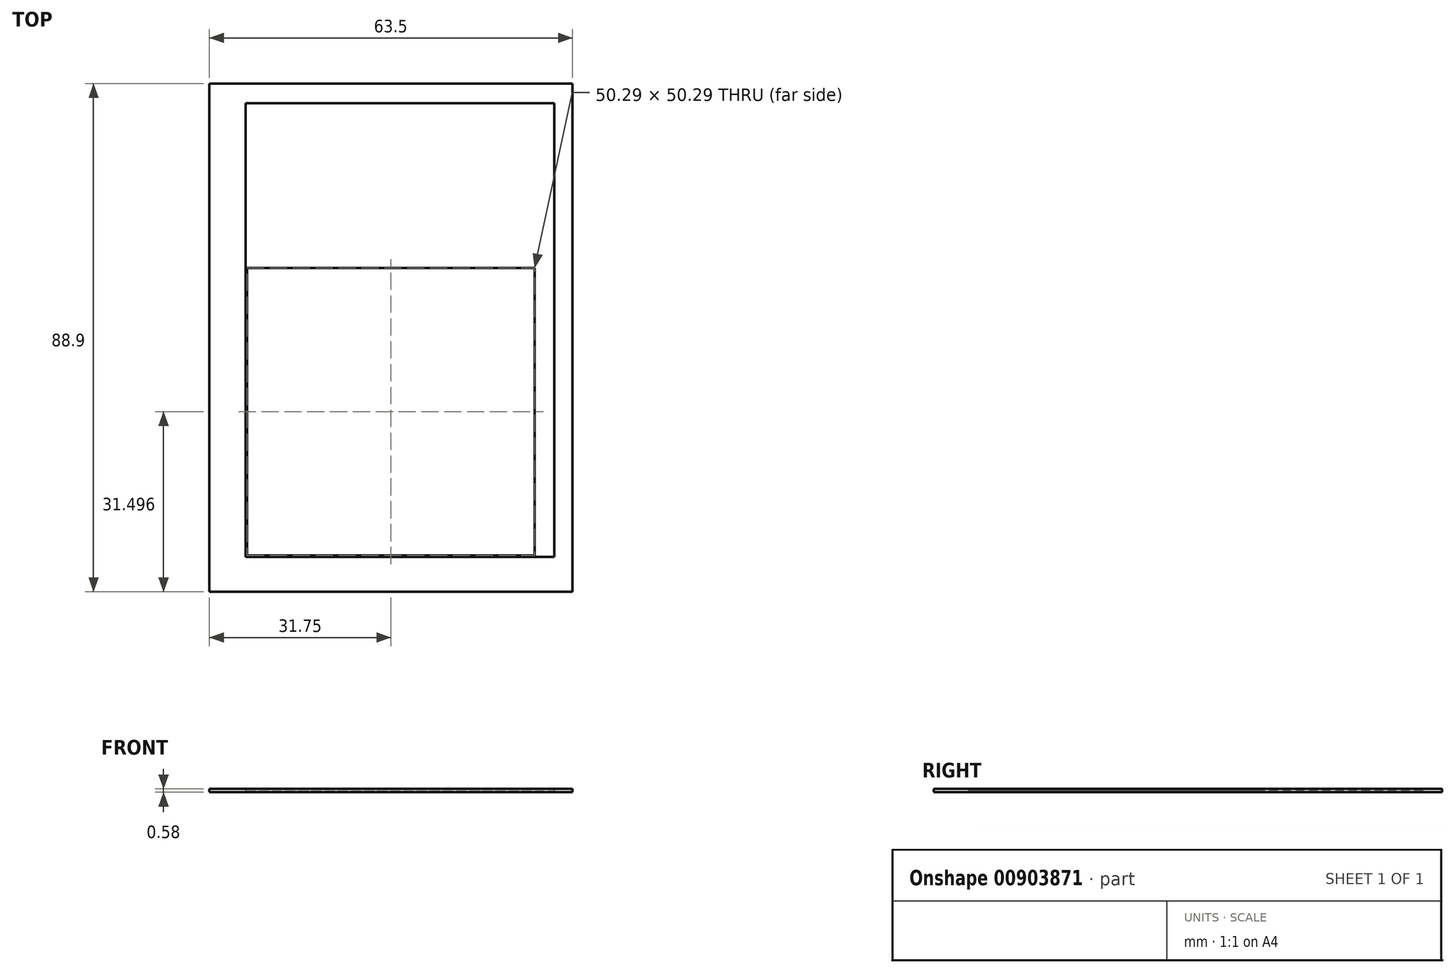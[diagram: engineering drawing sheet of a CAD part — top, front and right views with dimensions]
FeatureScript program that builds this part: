
annotation { "Feature Type Name" : "Feature", "Feature Type Description" : "" }
export const myFeature = defineFeature(function(context is Context, id is Id, definition is map)
    precondition{}
    {
        {
            var Q0;
            Q0=qCreatedBy(makeId("Top.planeOp"),FACE);
            var sketch = newSketch(context, id + "F0", { "sketchPlane" : qUnion([Q0])});
            skLineSegment(sketch, "E0.bottom", {"start": v(-25.15, 56.64) * mm, "end": v(25.15, 56.64) * mm});
            skLineSegment(sketch, "E0.top", {"start": v(-25.15, 6.35) * mm, "end": v(25.15, 6.35) * mm});
            skLineSegment(sketch, "E0.left", {"start": v(-25.15, 56.64) * mm, "end": v(-25.15, 6.35) * mm});
            skLineSegment(sketch, "E0.right", {"start": v(25.15, 56.64) * mm, "end": v(25.15, 6.35) * mm});
            skLineSegment(sketch, "E1.bottom", {"start": v(-31.75, 88.9) * mm, "end": v(31.75, 88.9) * mm});
            skLineSegment(sketch, "E1.top", {"start": v(-31.75, 0) * mm, "end": v(31.75, 0) * mm});
            skLineSegment(sketch, "E1.left", {"start": v(-31.75, 88.9) * mm, "end": v(-31.75, 0) * mm});
            skLineSegment(sketch, "E1.right", {"start": v(31.75, 88.9) * mm, "end": v(31.75, 0) * mm});
            skPoint(sketch, "E2", {"position": v(0, 88.9) * mm});
            skPoint(sketch, "E3", {"position": v(0, 56.64) * mm});
            skSolve(sketch);
        }
        {
            var Q0;
            Q0 = qSketchRegion(id + "F0", true);
            extrude(context, id + "F1", {"entities" : qUnion([Q0]), "depth" : 0.2 * mm, "offsetDistance" : 25.4 * mm});
        }
        {
            var Q0;
            Q0=makeQuery(id+"F1.opExtrude","CAP_FACE",FACE,{"disambiguationData":[OSD([sQuery(id+"F0.wireOp",EDGE,"E0.bottom"),sQuery(id+"F0.wireOp",EDGE,"E0.top"),sQuery(id+"F0.wireOp",EDGE,"E0.left"),sQuery(id+"F0.wireOp",EDGE,"E0.right"),sQuery(id+"F0.wireOp",EDGE,"E1.bottom"),sQuery(id+"F0.wireOp",EDGE,"E1.top"),sQuery(id+"F0.wireOp",EDGE,"E1.left"),sQuery(id+"F0.wireOp",EDGE,"E1.right")])],"isStart":false});
            var sketch = newSketch(context, id + "F2", { "sketchPlane" : qUnion([Q0])});
            skLineSegment(sketch, "E4.bottom", {"start": v(-25.4, 85.47) * mm, "end": v(28.58, 85.47) * mm});
            skLineSegment(sketch, "E4.top", {"start": v(-25.4, 6.1) * mm, "end": v(28.58, 6.1) * mm});
            skLineSegment(sketch, "E4.left", {"start": v(-25.4, 85.47) * mm, "end": v(-25.4, 6.1) * mm});
            skLineSegment(sketch, "E4.right", {"start": v(28.58, 85.47) * mm, "end": v(28.58, 6.1) * mm});
            skSolve(sketch);
        }
        {
            var Q0;
            Q0=makeQuery(id+"F2.imprint","IMPRINT",FACE,{"disambiguationData":[TD([[makeQuery(id+"F2.imprint","IMPRINT",EDGE,{"derivedFrom":sQuery(id+"F2.wireOp",EDGE,"E4.bottom")}),1.0]])]});
            extrude(context, id + "F3", {"entities" : qUnion([Q0]), "operationType" : NewBodyOperationType.ADD, "depth" : 0.38 * mm, "offsetDistance" : 25.4 * mm});
        }
    });
